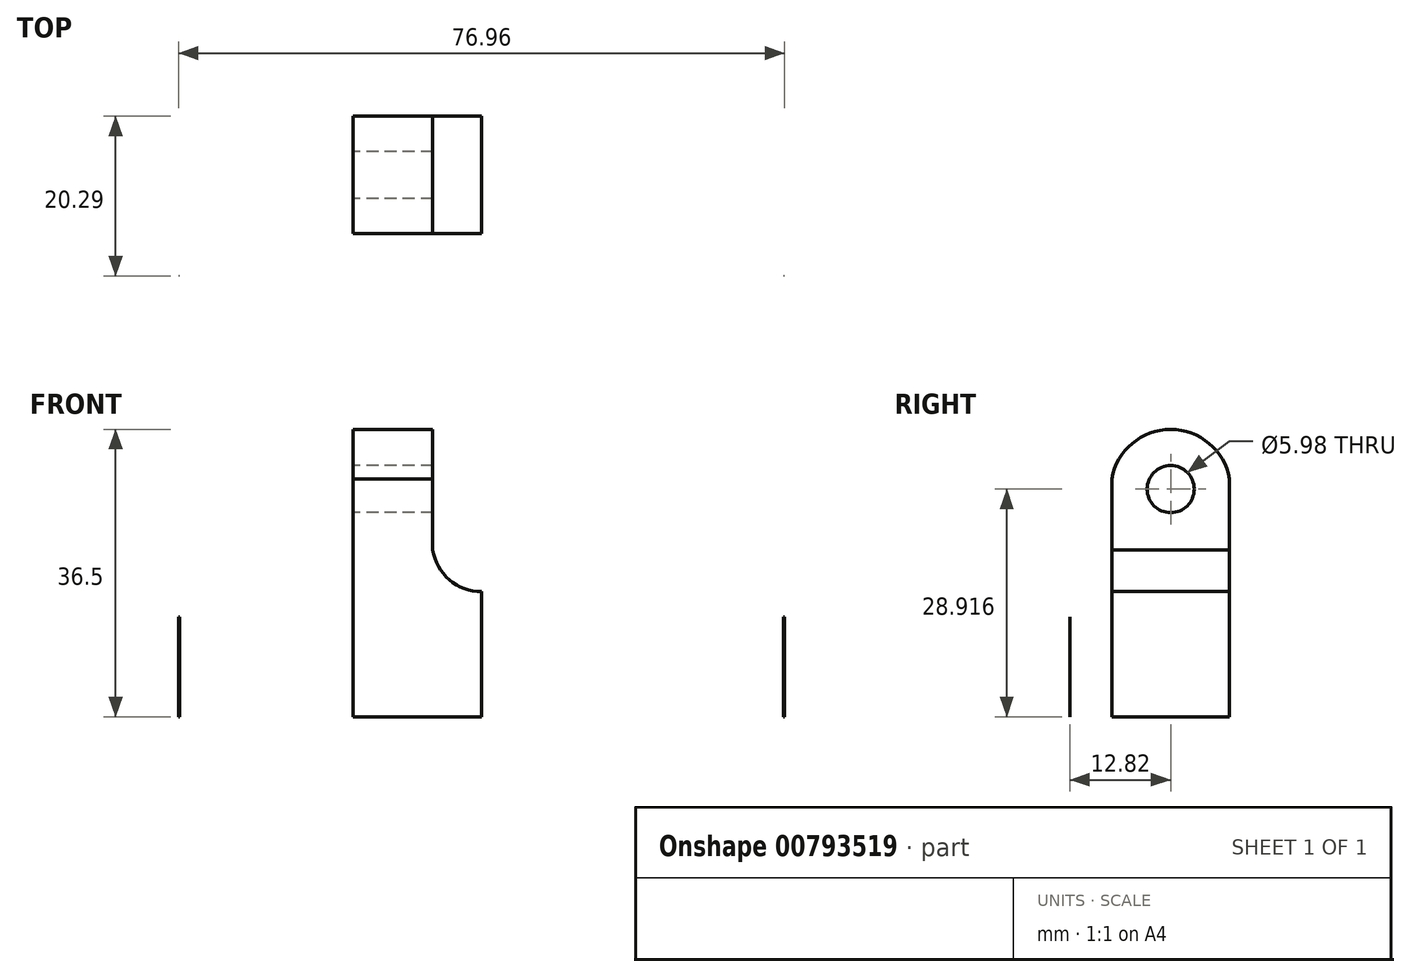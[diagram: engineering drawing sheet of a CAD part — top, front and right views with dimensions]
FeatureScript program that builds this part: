
annotation { "Feature Type Name" : "Feature", "Feature Type Description" : "" }
export const myFeature = defineFeature(function(context is Context, id is Id, definition is map)
    precondition{}
    {
        {
            var Q0;
            Q0=qCreatedBy(makeId("Top.planeOp"),FACE);
            var sketch = newSketch(context, id + "F0", { "sketchPlane" : qUnion([Q0])});
            skArc(sketch, "E0", {"start": v(-37.5, 12.69) * mm, "mid": v(-50.8, 0.26) * mm, "end": v(-38.02, -12.7) * mm});
            skCircle(sketch, "E1", {"center": v(-38.1, 0) * mm, "radius": 6.35 * mm});
            skLineSegment(sketch, "E2", {"start": v(-37.5, 12.69) * mm, "end": v(0.3, 12.7) * mm});
            skLineSegment(sketch, "E3", {"start": v(-38.18, -12.7) * mm, "end": v(0.3, -12.7) * mm});
            skLineSegment(sketch, "E4.bottom", {"start": v(-16.03, 7.6) * mm, "end": v(0.3, 7.6) * mm});
            skLineSegment(sketch, "E4.top", {"start": v(-16.03, -7.35) * mm, "end": v(0.3, -7.35) * mm});
            skLineSegment(sketch, "E4.left", {"start": v(-16.03, 7.6) * mm, "end": v(-16.03, -7.35) * mm});
            skLineSegment(sketch, "E5", {"start": v(0.3, 12.7) * mm, "end": v(0.3, -12.7) * mm});
            skSolve(sketch);
        }
        {
            var Q0;
            {var subQ1=sQuery(id+"F0.wireOp",EDGE,"E0");Q0=makeQuery(id+"F0.imprint","IMPRINT",FACE,{"disambiguationData":[TD([[makeQuery(id+"F0.imprint","IMPRINT",EDGE,{"derivedFrom":subQ1}),1.0]])]});}
            extrude(context, id + "F1", {"entities" : qUnion([Q0]), "depth" : 12.7 * mm, "offsetDistance" : 25.4 * mm});
        }
        {
            var Q0;
            {var subQ0=sQuery(id+"F0.wireOp",EDGE,"E4.bottom");Q0=makeQuery(id+"F0.imprint","IMPRINT",FACE,{"disambiguationData":[TD([[makeQuery(id+"F0.imprint","IMPRINT",EDGE,{"derivedFrom":subQ0}),-1.0]])]});}
            extrude(context, id + "F2", {"entities" : qUnion([Q0]), "operationType" : NewBodyOperationType.ADD, "depth" : 38.1 * mm, "offsetDistance" : 25.4 * mm});
        }
        {
            var Q0;
            Q0=makeQuery(id+"F2.opExtrude","SWEPT_FACE",FACE,{"disambiguationData":[OSD([sQuery(id+"F0.wireOp",EDGE,"E4.top")])]});
            var sketch = newSketch(context, id + "F3", { "sketchPlane" : qUnion([Q0])});
            skArc(sketch, "E6", {"start": v(-5.9, 21.2) * mm, "mid": v(-3.79, 17.4) * mm, "end": v(0.3, 15.9) * mm});
            skLineSegment(sketch, "E7", {"start": v(-5.9, 21.2) * mm, "end": v(-5.9, 38.1) * mm});
            skSolve(sketch);
        }
        {
            var Q0;
            {var subQ0=sQuery(id+"F3.wireOp",EDGE,"E6");Q0=makeQuery(id+"F3.imprint","IMPRINT",FACE,{"disambiguationData":[TD([[makeQuery(id+"F3.imprint","IMPRINT",EDGE,{"derivedFrom":subQ0}),1.0]])]});}
            extrude(context, id + "F4", {"entities" : qUnion([Q0]), "operationType" : NewBodyOperationType.REMOVE, "oppositeDirection" : true, "depth" : 25.4 * mm, "offsetDistance" : 25.4 * mm});
        }
        {
            var Q0;
            Q0=makeQuery(id+"F2.opExtrude","SWEPT_FACE",FACE,{"disambiguationData":[OSD([sQuery(id+"F0.wireOp",EDGE,"E4.left")])]});
            var sketch = newSketch(context, id + "F5", { "sketchPlane" : qUnion([Q0])});
            skArc(sketch, "E8", {"start": v(7.35, 30.22) * mm, "mid": v(-0.12, 36.5) * mm, "end": v(-7.6, 30.22) * mm});
            skCircle(sketch, "E9", {"center": v(-0.12, 28.92) * mm, "radius": 2.99 * mm});
            skSolve(sketch);
        }
        {
            var Q0;
            {var subQ0=sQuery(id+"F5.wireOp",EDGE,"E8");Q0=makeQuery(id+"F5.imprint","IMPRINT",FACE,{"disambiguationData":[TD([[makeQuery(id+"F5.imprint","IMPRINT",EDGE,{"derivedFrom":subQ0}),-1.0]])]});}
            extrude(context, id + "F6", {"entities" : qUnion([Q0]), "operationType" : NewBodyOperationType.REMOVE, "oppositeDirection" : true, "depth" : 25.4 * mm, "offsetDistance" : 25.4 * mm});
        }
        {
            var Q0;
            Q0=makeQuery(id+"F5.imprint","IMPRINT",FACE,{"disambiguationData":[TD([[makeQuery(id+"F5.imprint","IMPRINT",EDGE,{"derivedFrom":sQuery(id+"F5.wireOp",EDGE,"E9")}),1.0]])]});
            extrude(context, id + "F7", {"entities" : qUnion([Q0]), "operationType" : NewBodyOperationType.REMOVE, "oppositeDirection" : true, "depth" : 25.4 * mm, "offsetDistance" : 25.4 * mm});
        }
        {
            var Q0;
            Q0=makeQuery(id+"F1.opExtrude","SWEPT_BODY",BODY,{"disambiguationData":[OSD([sQuery(id+"F0.wireOp",EDGE,"E0"),sQuery(id+"F0.wireOp",EDGE,"E1"),sQuery(id+"F0.wireOp",EDGE,"E2"),sQuery(id+"F0.wireOp",EDGE,"E3"),sQuery(id+"F0.wireOp",EDGE,"E4.bottom"),sQuery(id+"F0.wireOp",EDGE,"E4.top"),sQuery(id+"F0.wireOp",EDGE,"E4.left"),sQuery(id+"F0.wireOp",EDGE,"E5")])]});
            var Q1;
            {var subQ0=sQuery(id+"F0.wireOp",EDGE,"E5");Q1=makeQuery(id+"F2.boolean.opBoolean","MERGE",FACE,{"derivedFrom":[makeQuery(id+"F1.opExtrude","SWEPT_FACE",FACE,{"disambiguationData":[OSD([subQ0]),TDD([makeQuery(id+"F0.imprint","IMPRINT",EDGE,{"disambiguationData":[TD([[makeQuery(id+"F0.imprint","INTERSECT",VERTEX,{"derivedFrom":[sQuery(id+"F0.wireOp",EDGE,"E2"),subQ0]}),-1.0]])],"derivedFrom":subQ0})])]}),makeQuery(id+"F1.opExtrude","SWEPT_FACE",FACE,{"disambiguationData":[OSD([subQ0]),TDD([makeQuery(id+"F0.imprint","IMPRINT",EDGE,{"disambiguationData":[TD([[makeQuery(id+"F0.imprint","INTERSECT",VERTEX,{"derivedFrom":[sQuery(id+"F0.wireOp",EDGE,"E3"),subQ0]}),1.0]])],"derivedFrom":subQ0})])]}),makeQuery(id+"F2.opExtrude","SWEPT_FACE",FACE,{"disambiguationData":[OSD([subQ0])]})]});}
            mirror(context, id + "F8", {"operationType" : NewBodyOperationType.ADD, "entities" : qUnion([Q0]), "mirrorPlane" : qUnion([Q1])});
        }
    });
